# Revit family: 728-202041xxxxxx
name_source: partatom
category: Leuchten
units: mm (PartAtom-declared; Revit-internal decimal feet)

## family parameters
Arbeitsebenenbasiert = Nein
Beim Laden mit Abzugskörper schneiden = Nein
Bemaßung runder Anschluss = Durchmesser verwenden
Gemeinsam genutzt = Nein
Immer vertikal = Ja
Lichtquelle = Ja
Raumberechnungspunkt = Nein
Teiletyp = Normal

## types (1)
- Norm
    Angeforderte Genauigkeit = Niedrig
    Bauteilnummer = ENG000018595
    Benutzerstatus = Freigegeben
    Beschreibung = _Simple
    Bestandsnummer = Simple
    Datei für fotometrisches Netz = 728-20204111355d_LOG OUT 2.1 PD HE 16W 2700K OPAL - weiss - DEKO weiss DALI-1277353.ies
    Datum Konstruktionsgenehmigung = 25.02.2020 12:51:22
    Dichte = 1060,00 kg/m³
    Erstellungsdatum = 13.02.2020 00:00:00
    Farbfilter = 16777215
    Farbtemperaturverschiebung bei Dämpfen der Lampe = <Keine Auswahl>
    Fläche = 1,51 m²
    Konstruktionsstatus = 1
    Masse = 1,50 kg
    MatchCode = 728-202041%;728-202__1______;728-202__1__x___;728-_________xx_
    Material = _ acc. techn. INFO
    Neigungswinkel = 90,00°
    Projekt = 728-202041xxxxxx
    Revisionsnummer = 00
    Rohabmessungen = Ja
    Speicherpfad = 728-LogOut-2v1\M-CAD\Vereinfachung\728-202041xxxxxx HL UGR 4ft
    VDS_Category = Inventor Bauteil
    VDS_NumSchm = MoltoLuce
    Volumen = 0,00 m³
    Von Linienlänge aussenden = 1120 mm  [stored 3.67454 ft]
    Vorgabe-Ansicht = 0 mm  [stored 0 ft]

note: [stored X ft] marks values corroborated as IEEE doubles in the binary element streams (Revit-internal decimal feet)
